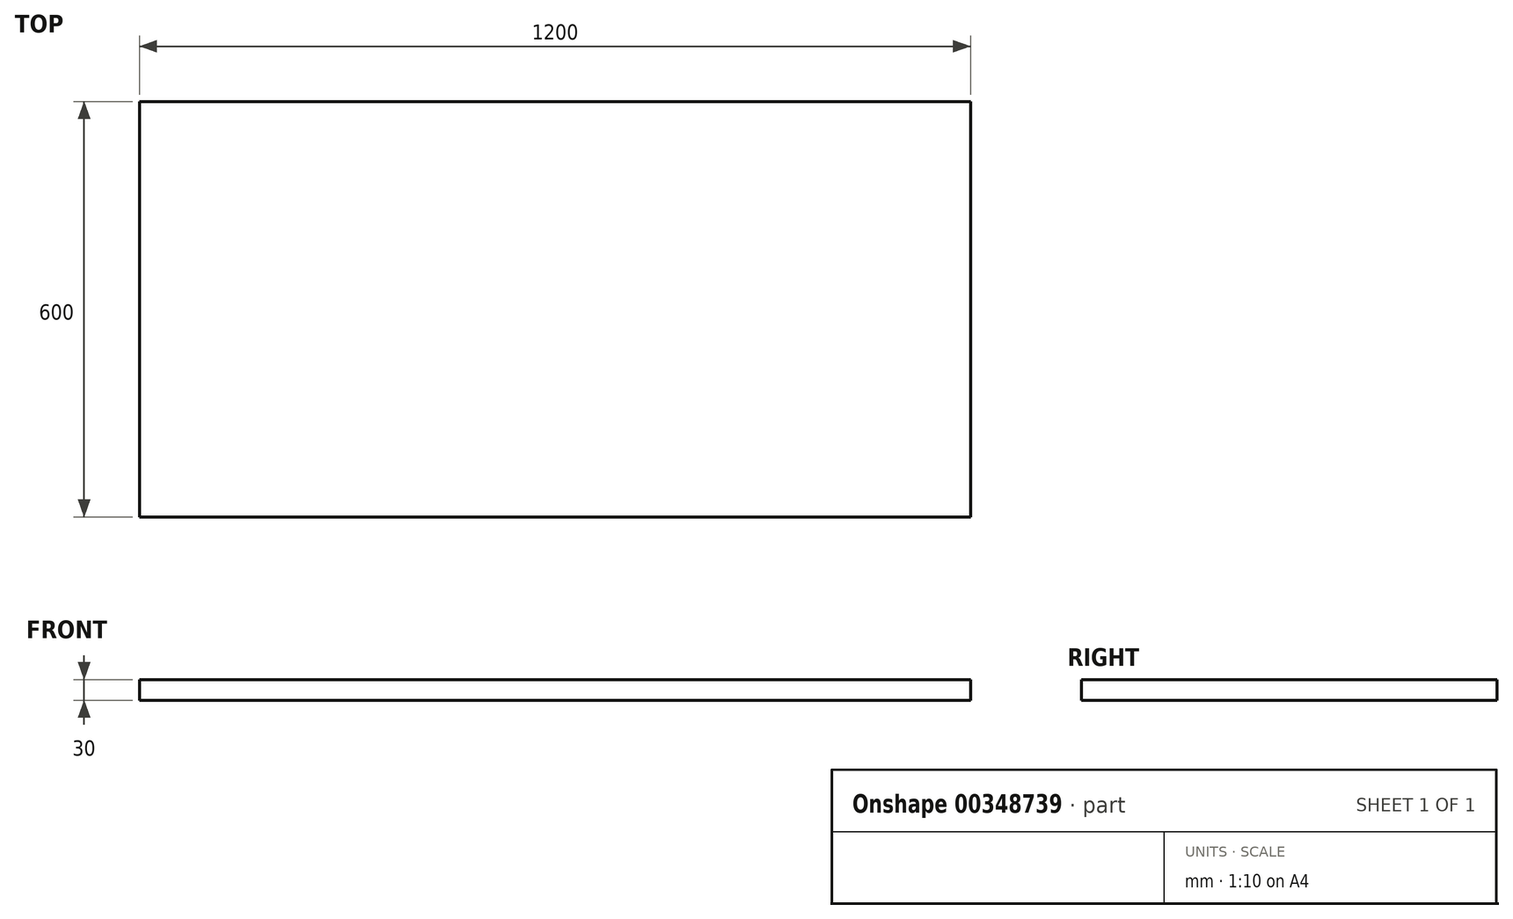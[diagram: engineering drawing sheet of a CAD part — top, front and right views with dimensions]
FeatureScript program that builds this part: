
annotation { "Feature Type Name" : "Feature", "Feature Type Description" : "" }
export const myFeature = defineFeature(function(context is Context, id is Id, definition is map)
    precondition{}
    {
        {
            var Q0;
            Q0=qCreatedBy(makeId("Top.planeOp"),FACE);
            var sketch = newSketch(context, id + "F0", { "sketchPlane" : qUnion([Q0])});
            skLineSegment(sketch, "E0.bottom", {"start": v(-166.63, 477.29) * mm, "end": v(1033.37, 477.29) * mm});
            skLineSegment(sketch, "E0.top", {"start": v(-166.63, -122.71) * mm, "end": v(1033.37, -122.71) * mm});
            skLineSegment(sketch, "E0.left", {"start": v(-166.63, 477.29) * mm, "end": v(-166.63, -122.71) * mm});
            skLineSegment(sketch, "E0.right", {"start": v(1033.37, 477.29) * mm, "end": v(1033.37, -122.71) * mm});
            skSolve(sketch);
        }
        {
            var Q0;
            Q0 = qSketchRegion(id + "F0", true);
            extrude(context, id + "F1", {"entities" : qUnion([Q0]), "depth" : 30 * mm});
        }
    });
